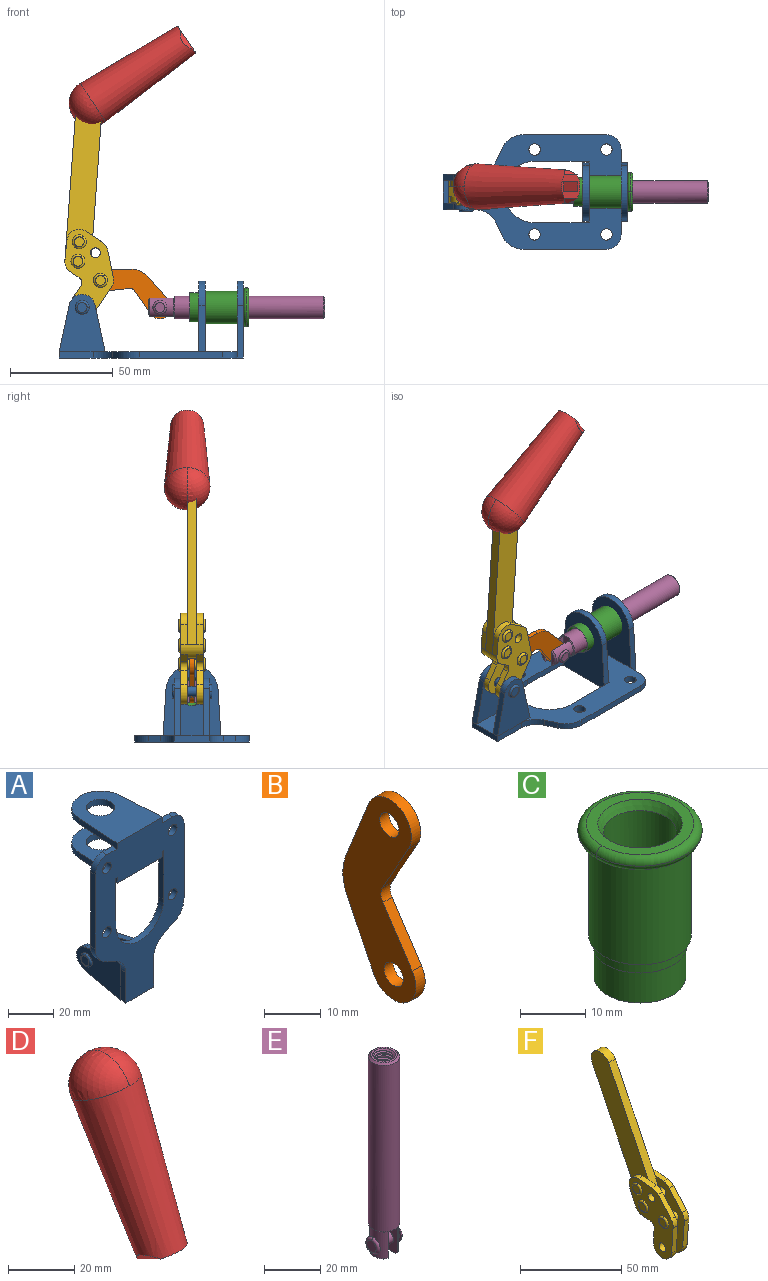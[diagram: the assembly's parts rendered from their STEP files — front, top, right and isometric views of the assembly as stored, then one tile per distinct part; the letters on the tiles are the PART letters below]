
ASSEMBLY  parts=6 mates=6
PART A: 55 faces, bbox 55.7x37.4x89.8 mm
  f0: torus R=2.41mm, axis (-1,0,0), area 15mm2, adj f11,f15,f25
  f1: torus R=2.41mm, axis (-1,0,0), area 15mm2, adj f10,f12,f22
  f2: cylinder r=2.78mm len=5.56mm, axis (0,-1,0), area 54.2mm2, adj f30,f54
  f3: cylinder r=14.99mm len=29.97mm, axis (0,-1,0), area 145.9mm2, adj f30,f49,f53,f54
  f4: cylinder r=2.78mm len=5.56mm, axis (0,-1,0), area 54.2mm2, adj f30,f54
  f5: cylinder r=2.78mm len=5.56mm, axis (0,-1,0), area 54.2mm2, adj f30,f54
  f6: cylinder r=2.78mm len=5.56mm, axis (0,-1,0), area 54.2mm2, adj f30,f54
  f7: cylinder r=6.35mm len=12.7mm, axis (0,0,1), area 123.6mm2, adj f27,f51
  f8: cylinder r=6.35mm len=12.7mm, axis (0,0,-1), area 124.7mm2, adj f21,f35
  f9: cylinder r=2.41mm len=11.18mm, axis (-1,0,0), area 169.4mm2, adj f16,f19
  f10: plane 4.83x4.83mm, normal (1,0,0), area 18.3mm2, adj f1,f12
  f11: plane 4.83x4.83mm, normal (-1,0,0), area 18.3mm2, adj f0,f15
  f12: torus R=2.41mm, axis (-1,0,0), area 15mm2, adj f1,f10,f22
  f13: cylinder r=6.35mm len=12.41mm, axis (1,0,0), area 53.4mm2, adj f18,f19,f22,f23
  f14: cylinder r=6.35mm len=12.41mm, axis (-1,0,0), area 53.4mm2, adj f16,f17,f24,f25
  f15: torus R=2.41mm, axis (-1,0,0), area 15mm2, adj f0,f11,f25
  f16: plane 27.86x22.35mm, normal (1,0,0), area 425.4mm2, adj f9,f14,f17,f24,f30
  f17: plane 22.86x4.97mm, normal (0,0.21,0.98), area 72.5mm2, adj f14,f16,f25,f30
  f18: plane 22.86x4.97mm, normal (0,0.21,0.98), area 72.5mm2, adj f13,f19,f22,f30
  f19: plane 27.86x22.35mm, normal (-1,0,0), area 425.4mm2, adj f9,f13,f18,f23,f30
  f20: cylinder r=12.7mm len=25.35mm, axis (0,0,-1), area 119.8mm2, adj f21,f34,f35,f36
  f21: plane 34.21x28.07mm, normal (0,0,-1), area 702.4mm2, adj f8,f20,f30,f34,f36
  f22: plane 27.96x22.45mm, normal (1,0,0), area 407.2mm2, adj f1,f12,f13,f18,f23,f30,f42,f43
  f23: plane 22.86x4.97mm, normal (0,0.21,-0.98), area 72.5mm2, adj f13,f19,f22,f44
  f24: plane 22.86x4.97mm, normal (0,0.21,-0.98), area 72.5mm2, adj f14,f16,f25,f44
  f25: plane 27.86x22.35mm, normal (-1,0,0), area 407.1mm2, adj f0,f14,f15,f17,f24,f30,f45,f46
  f26: plane 3.1x0.95mm, normal (0,0,-1), area 2.7mm2, adj f30,f49,f50,f54
  f27: plane 34.21x28.07mm, normal (0,0,1), area 702.4mm2, adj f7,f28,f30,f50,f52
  f28: cylinder r=12.7mm len=25.35mm, axis (0,0,1), area 118.8mm2, adj f27,f50,f51,f52
  f29: plane 3.1x0.95mm, normal (0,0,-1), area 2.7mm2, adj f30,f52,f53,f54
  f30: plane 86.54x55.63mm, normal (0,1,0), area 2362.9mm2, adj f2,f3,f4,f5,f6,f16,f17,f18
  f31: plane 40.56x3.1mm, normal (-1,0,0), area 125.7mm2, adj f30,f32,f48,f54
  f32: cylinder r=7.11mm len=7.11mm, axis (0,-1,0), area 34.6mm2, adj f30,f31,f33,f54
  f33: plane 6.67x3.1mm, normal (0,0,1), area 20.4mm2, adj f30,f32,f34,f54
  f34: plane 25.39x3.13mm, normal (-1,0.06,0), area 79.5mm2, adj f20,f21,f33,f35,f54
  f35: plane 37.31x28.45mm, normal (0,0,1), area 789.9mm2, adj f8,f20,f34,f36,f54
  f36: plane 25.39x3.13mm, normal (1,0.06,0), area 79.5mm2, adj f20,f21,f35,f37,f54
  f37: plane 6.67x3.1mm, normal (0,0,1), area 20.4mm2, adj f30,f36,f38,f54
  f38: cylinder r=7.11mm len=7.11mm, axis (0,-1,0), area 34.6mm2, adj f30,f37,f39,f54
  f39: plane 40.56x3.1mm, normal (1,0,0), area 125.7mm2, adj f30,f38,f40,f54
  f40: cylinder r=11.18mm len=10.16mm, axis (0,-1,0), area 39.5mm2, adj f30,f39,f41,f54
  f41: plane 6.09x3.1mm, normal (0.42,0,-0.91), area 20.8mm2, adj f30,f40,f42,f54
  f42: cylinder r=11.18mm len=9.41mm, axis (0,-1,0), area 37.2mm2, adj f22,f30,f41,f43,f54
  f43: plane 16.5x3.1mm, normal (1,0,0), area 51.1mm2, adj f22,f42,f44,f54
  f44: plane 17.37x3.1mm, normal (0,0,-1), area 53.8mm2, adj f23,f24,f30,f43,f45,f54
  f45: plane 16.5x3.1mm, normal (-1,0,0), area 51.1mm2, adj f25,f44,f46,f54
  f46: cylinder r=11.18mm len=9.41mm, axis (0,-1,0), area 37.2mm2, adj f25,f30,f45,f47,f54
  f47: plane 6.09x3.1mm, normal (-0.42,0,-0.91), area 20.8mm2, adj f30,f46,f48,f54
  f48: cylinder r=11.18mm len=10.16mm, axis (0,-1,0), area 39.5mm2, adj f30,f31,f47,f54
  f49: plane 26.54x3.1mm, normal (-1,0,0), area 82.3mm2, adj f3,f26,f30,f54
  f50: plane 25.39x3.1mm, normal (1,0.06,0), area 78.8mm2, adj f26,f27,f28,f51,f54
  f51: plane 37.31x28.45mm, normal (0,0,-1), area 789.9mm2, adj f7,f28,f50,f52,f54
  f52: plane 25.39x3.1mm, normal (-1,0.06,0), area 78.8mm2, adj f27,f28,f29,f51,f54
  f53: plane 26.54x3.1mm, normal (1,0,0), area 82.3mm2, adj f3,f29,f30,f54
  f54: plane 89.66x55.63mm, normal (0,-1,0), area 2678.5mm2, adj f2,f3,f4,f5,f6,f26,f29,f31
PART B: 12 faces, bbox 2.3x18.2x42.8 mm
  f0: cylinder r=2.4mm len=4.8mm, axis (1,0,0), area 34.9mm2, adj f4,f11
  f1: cylinder r=10.41mm len=8.47mm, axis (1,0,0), area 20.2mm2, adj f4,f9,f10,f11
  f2: cylinder r=3.05mm len=3.16mm, axis (1,0,0), area 7.7mm2, adj f4,f6,f7,f11
  f3: cylinder r=2.4mm len=4.8mm, axis (1,0,0), area 34.9mm2, adj f4,f11
  f4: plane 42.81x18.23mm, normal (-1,0,0), area 414.1mm2, adj f0,f1,f2,f3,f5,f6,f7,f8
  f5: cylinder r=5.54mm len=10.67mm, axis (1,0,0), area 41.8mm2, adj f4,f6,f10,f11
  f6: plane 11.66x6.53mm, normal (0,-0.87,-0.49), area 30.9mm2, adj f2,f4,f5,f11
  f7: plane 11.17x7.33mm, normal (0,-0.84,0.55), area 30.9mm2, adj f2,f4,f8,f11
  f8: cylinder r=5.54mm len=10.51mm, axis (1,0,0), area 41.8mm2, adj f4,f7,f9,f11
  f9: plane 13.67x6.67mm, normal (0,0.9,-0.44), area 35.1mm2, adj f1,f4,f8,f11
  f10: plane 14.1x5.7mm, normal (0,0.93,0.37), area 35.1mm2, adj f1,f4,f5,f11
  f11: plane 42.81x18.23mm, normal (1,0,0), area 414.1mm2, adj f0,f1,f2,f3,f5,f6,f7,f8
PART C: 15 faces, bbox 20.6x20.6x28.7 mm
  f0: torus R=8.26mm, axis (0,0,1), area 56.8mm2, adj f1,f10,f12
  f1: torus R=8.26mm, axis (0,0,1), area 56.8mm2, adj f0,f6,f13
  f2: cylinder r=5.59mm len=25.91mm, axis (0,0,1), area 909.6mm2, adj f3,f4
  f3: cone r=6.86mm half-angle=45deg, axis (0,0,-1), area 70.2mm2, adj f2,f14
  f4: cone r=6.47mm half-angle=30deg, axis (0,0,1), area 66.7mm2, adj f2,f13
  f5: cylinder r=7.04mm len=14.07mm, axis (0,0,1), area 252.6mm2, adj f11,f14
  f6: torus R=8.26mm, axis (0,0,1), area 56.8mm2, adj f1,f12,f13
  f7: cylinder r=7.16mm len=14.33mm, axis (0,0,1), area 91.5mm2, adj f9,f11
  f8: cylinder r=7.86mm len=18.42mm, axis (0,0,1), area 909.6mm2, adj f9,f10
  f9: plane 15.72x15.72mm, normal (0,0,-1), area 33mm2, adj f7,f8
  f10: plane 16.51x16.51mm, normal (0,0,-1), area 19.9mm2, adj f0,f8,f12
  f11: plane 14.33x14.33mm, normal (0,0,-1), area 5.7mm2, adj f5,f7
  f12: torus R=8.26mm, axis (0,0,1), area 56.8mm2, adj f0,f6,f10
  f13: plane 16.51x16.51mm, normal (0,0,1), area 82.7mm2, adj f1,f4,f6
  f14: plane 14.07x14.07mm, normal (0,0,-1), area 7.8mm2, adj f3,f5
PART D: 11 faces, bbox 22.3x42.6x64.5 mm
  f0: sphere r=11.13mm, area 411.4mm2, adj f1,f8
  f1: cone r=11.11mm half-angle=3.3deg, axis (0,0.44,0.9), area 3251.8mm2, adj f0,f7,f8,f9,f10
  f2: cylinder r=6.16mm len=11.7mm, axis (1,0,0), area 89.5mm2, adj f3,f4,f5,f6
  f3: plane 60.23x36.75mm, normal (-1,0,0), area 763.6mm2, adj f2,f4,f6,f10
  f4: plane 51.37x25.05mm, normal (0,0.9,-0.44), area 264.2mm2, adj f2,f3,f5,f10
  f5: plane 60.23x36.75mm, normal (1,0,0), area 763.6mm2, adj f2,f4,f6,f10
  f6: plane 51.37x25.05mm, normal (0,-0.9,0.44), area 264.2mm2, adj f2,f3,f5,f10
  f7: plane 9.95x5.95mm, normal (0.71,-0.31,-0.64), area 25.8mm2, adj f1,f10
  f8: sphere r=11.13mm, area 411.4mm2, adj f0,f1
  f9: plane 9.95x5.95mm, normal (-0.71,-0.31,-0.64), area 25.8mm2, adj f1,f10
  f10: plane 14.27x11.38mm, normal (0,-0.44,-0.9), area 106.7mm2, adj f1,f3,f4,f5,f6,f7,f9
PART E: 48 faces, bbox 12.6x11.1x86.1 mm
  f0: torus R=2.41mm, axis (-1,0,0), area 15mm2, adj f30,f32,f34
  f1: torus R=2.41mm, axis (-1,0,0), area 15mm2, adj f29,f31,f33
  f2: cylinder r=5.54mm len=72.39mm, axis (0,0,1), area 2518.5mm2, adj f3,f4,f42,f43
  f3: cone r=5.54mm half-angle=45deg, axis (0,0,1), area 7.6mm2, adj f2,f5,f41
  f4: cone r=5.54mm half-angle=45deg, axis (0,0,-1), area 34.9mm2, adj f2,f39
  f5: cylinder r=5.08mm len=11.48mm, axis (0,0,1), area 108.3mm2, adj f3,f7,f8,f41
  f6: cylinder r=2.41mm len=4.83mm, axis (-1,0,0), area 71.2mm2, adj f40,f41
  f7: cylinder r=2.41mm len=4.83mm, axis (-1,0,0), area 7.6mm2, adj f5,f34
  f8: cone r=5.08mm half-angle=45deg, axis (0,0,1), area 10.6mm2, adj f5,f37,f41
  f9: cone r=3.98mm half-angle=45deg, axis (0,0,1), area 17.6mm2, adj f27,f39,f45,f46,f47
  f10: cylinder r=2.41mm len=4.83mm, axis (-1,0,0), area 7.6mm2, adj f33,f38
  f11: cylinder r=3.2mm len=6.4mm, axis (0,0,1), area 78.4mm2, adj f12,f28,f44,f45,f47
  f12: cylinder r=3.2mm len=6.4mm, axis (0,0,1), area 10.5mm2, adj f11,f13,f45,f47
  f13: cylinder r=3.2mm len=6.4mm, axis (0,0,1), area 10.5mm2, adj f12,f14,f45,f47
  f14: cylinder r=3.2mm len=6.4mm, axis (0,0,1), area 10.5mm2, adj f13,f15,f45,f47
  f15: cylinder r=3.2mm len=6.4mm, axis (0,0,1), area 10.5mm2, adj f14,f16,f45,f47
  f16: cylinder r=3.2mm len=6.4mm, axis (0,0,1), area 10.5mm2, adj f15,f17,f45,f47
  f17: cylinder r=3.2mm len=6.4mm, axis (0,0,1), area 10.5mm2, adj f16,f18,f45,f47
  f18: cylinder r=3.2mm len=6.4mm, axis (0,0,1), area 10.5mm2, adj f17,f19,f45,f47
  f19: cylinder r=3.2mm len=6.4mm, axis (0,0,1), area 10.5mm2, adj f18,f20,f45,f47
  f20: cylinder r=3.2mm len=6.4mm, axis (0,0,1), area 10.5mm2, adj f19,f21,f45,f47
  f21: cylinder r=3.2mm len=6.4mm, axis (0,0,1), area 10.5mm2, adj f20,f22,f45,f47
  f22: cylinder r=3.2mm len=6.4mm, axis (0,0,1), area 10.5mm2, adj f21,f23,f45,f47
  f23: cylinder r=3.2mm len=6.4mm, axis (0,0,1), area 10.5mm2, adj f22,f24,f45,f47
  f24: cylinder r=3.2mm len=6.4mm, axis (0,0,1), area 10.5mm2, adj f23,f25,f45,f47
  f25: cylinder r=3.2mm len=6.4mm, axis (0,0,1), area 10.5mm2, adj f24,f26,f45,f47
  f26: cylinder r=3.2mm len=6.4mm, axis (0,0,1), area 10.5mm2, adj f25,f27,f45,f47
  f27: cylinder r=3.2mm len=6.4mm, axis (0,0,1), area 7.4mm2, adj f9,f26,f45,f47
  f28: cone r=3.2mm half-angle=60deg, axis (0,0,1), area 37.2mm2, adj f11
  f29: plane 4.83x4.83mm, normal (-1,0,0), area 18.3mm2, adj f1,f31
  f30: plane 4.83x4.83mm, normal (1,0,0), area 18.3mm2, adj f0,f32
  f31: torus R=2.41mm, axis (-1,0,0), area 15mm2, adj f1,f29,f33
  f32: torus R=2.41mm, axis (-1,0,0), area 15mm2, adj f0,f30,f34
  f33: plane 6.83x6.83mm, normal (1,0,0), area 18.3mm2, adj f1,f10,f31
  f34: plane 6.83x6.83mm, normal (-1,0,0), area 18.3mm2, adj f0,f7,f32
  f35: cone r=5.08mm half-angle=45deg, axis (0,0,1), area 10.6mm2, adj f36,f38,f40
  f36: plane 7.25x1.97mm, normal (0,0,-1), area 10mm2, adj f35,f40
  f37: plane 7.25x1.97mm, normal (0,0,-1), area 10mm2, adj f8,f41
  f38: cylinder r=5.08mm len=11.48mm, axis (0,0,1), area 108.3mm2, adj f10,f35,f40,f42
  f39: plane 9.55x9.55mm, normal (0,0,1), area 22mm2, adj f4,f9
  f40: plane 12.76x10.09mm, normal (1,0,0), area 95.7mm2, adj f6,f35,f36,f38,f42,f43
  f41: plane 12.76x10.09mm, normal (-1,0,0), area 95.7mm2, adj f3,f5,f6,f8,f37,f43
  f42: cone r=5.54mm half-angle=45deg, axis (0,0,1), area 7.6mm2, adj f2,f38,f40
  f43: plane 11.07x4.7mm, normal (0,0,-1), area 50.4mm2, adj f2,f40,f41
  f44: plane 0.89x0.62mm, normal (-1,0,0), area 0.3mm2, adj f11,f45,f46,f47
  f45: bspline ~24.8x7.63mm, area 266.6mm2, adj f9,f11,f12,f13,f14,f15,f16,f17
  f46: bspline ~24.87x7.63mm, area 73.6mm2, adj f9,f44,f45,f47
  f47: bspline ~24.98x7.63mm, area 272.5mm2, adj f9,f11,f12,f13,f14,f15,f16,f17
PART F: 59 faces, bbox 12.9x60.2x99.6 mm
  f0: torus R=2.39mm, axis (-1,0,0), area 14.9mm2, adj f20,f43,f51
  f1: torus R=2.39mm, axis (-1,0,0), area 14.9mm2, adj f19,f42,f51
  f2: torus R=2.39mm, axis (-1,0,0), area 14.9mm2, adj f18,f35,f51
  f3: torus R=2.39mm, axis (-1,0,0), area 14.9mm2, adj f14,f17,f23
  f4: torus R=2.39mm, axis (-1,0,0), area 14.9mm2, adj f13,f16,f23
  f5: torus R=2.39mm, axis (-1,0,0), area 14.9mm2, adj f12,f15,f23
  f6: cylinder r=2.39mm len=4.78mm, axis (1,0,0), area 46.5mm2, adj f48,f50,f51
  f7: cylinder r=2.39mm len=4.78mm, axis (1,0,0), area 46.5mm2, adj f50,f51
  f8: cylinder r=6.35mm len=12.68mm, axis (1,0,0), area 61.8mm2, adj f38,f39,f50,f51
  f9: cylinder r=2.39mm len=4.78mm, axis (-1,0,0), area 70.5mm2, adj f46,f50
  f10: cylinder r=2.39mm len=4.78mm, axis (-1,0,0), area 46.5mm2, adj f23,f45,f46
  f11: cylinder r=2.39mm len=4.78mm, axis (-1,0,0), area 46.5mm2, adj f23,f46
  f12: plane 4.78x4.78mm, normal (1,0,0), area 17.9mm2, adj f5,f15
  f13: plane 4.78x4.78mm, normal (1,0,0), area 17.9mm2, adj f4,f16
  f14: plane 4.78x4.78mm, normal (1,0,0), area 17.9mm2, adj f3,f17
  f15: torus R=2.39mm, axis (-1,0,0), area 14.9mm2, adj f5,f12,f23
  f16: torus R=2.39mm, axis (-1,0,0), area 14.9mm2, adj f4,f13,f23
  f17: torus R=2.39mm, axis (-1,0,0), area 14.9mm2, adj f3,f14,f23
  f18: plane 4.78x4.78mm, normal (-1,0,0), area 17.9mm2, adj f2,f35
  f19: plane 4.78x4.78mm, normal (-1,0,0), area 17.9mm2, adj f1,f42
  f20: plane 4.78x4.78mm, normal (-1,0,0), area 17.9mm2, adj f0,f43
  f21: plane 2.26x0.2mm, normal (1,0,0), area 0.2mm2, adj f31,f44
  f22: plane 2.26x0.2mm, normal (-1,0,0), area 0.2mm2, adj f41,f44
  f23: plane 39.37x30.77mm, normal (1,0,0), area 565.5mm2, adj f3,f4,f5,f10,f11,f15,f16,f17
  f24: cylinder r=6.1mm len=4.15mm, axis (-1,0,0), area 14.7mm2, adj f23,f25,f32,f46
  f25: plane 10.25x9.01mm, normal (0,-0.75,0.66), area 42.3mm2, adj f23,f24,f26,f46
  f26: cylinder r=6.35mm len=4.64mm, axis (-1,0,0), area 15.6mm2, adj f23,f25,f27,f46
  f27: plane 15.84x3.1mm, normal (0,-1,-0.07), area 49.2mm2, adj f23,f26,f28,f46
  f28: cylinder r=6.35mm len=12.68mm, axis (-1,0,0), area 61.8mm2, adj f23,f27,f29,f46
  f29: plane 8.11x3.1mm, normal (0,1,0.07), area 25.2mm2, adj f23,f28,f30,f46
  f30: cylinder r=3.05mm len=3.25mm, axis (-1,0,0), area 14.8mm2, adj f23,f29,f31,f46
  f31: plane 5.99x3.1mm, normal (0,0.07,-1), area 18.6mm2, adj f21,f23,f30,f44,f46
  f32: plane 9.5x3.1mm, normal (0,-0.07,1), area 29.5mm2, adj f23,f24,f33,f46,f47
  f33: cylinder r=6.1mm len=8.63mm, axis (-1,0,0), area 39.1mm2, adj f23,f32,f34,f47
  f34: plane 8.65x3.96mm, normal (0,0.91,-0.42), area 29.5mm2, adj f23,f33,f44,f47
  f35: torus R=2.39mm, axis (-1,0,0), area 14.9mm2, adj f2,f18,f51
  f36: plane 10.25x9.01mm, normal (0,-0.75,0.66), area 42.3mm2, adj f37,f49,f50,f51
  f37: cylinder r=6.35mm len=4.64mm, axis (1,0,0), area 15.6mm2, adj f36,f38,f50,f51
  f38: plane 15.84x3.1mm, normal (0,-1,-0.07), area 49.2mm2, adj f8,f37,f50,f51
  f39: plane 8.11x3.1mm, normal (0,1,0.07), area 25.2mm2, adj f8,f40,f50,f51
  f40: cylinder r=3.05mm len=3.25mm, axis (1,0,0), area 14.8mm2, adj f39,f41,f50,f51
  f41: plane 5.99x3.1mm, normal (0,0.07,-1), area 18.6mm2, adj f22,f40,f44,f50,f51
  f42: torus R=2.39mm, axis (-1,0,0), area 14.9mm2, adj f1,f19,f51
  f43: torus R=2.39mm, axis (-1,0,0), area 14.9mm2, adj f0,f20,f51
  f44: cylinder r=6.35mm len=12.12mm, axis (-1,0,0), area 128.9mm2, adj f21,f22,f23,f31,f34,f41,f46,f47
  f45: plane 2.65x1.35mm, normal (1,0,0), area 1mm2, adj f10,f55
  f46: plane 39.08x20.42mm, normal (-1,0,0), area 412.5mm2, adj f9,f10,f11,f24,f25,f26,f27,f28
  f47: plane 77.62x39.82mm, normal (1,0,0), area 850mm2, adj f32,f33,f34,f44,f53,f54,f55
  f48: plane 2.65x1.35mm, normal (-1,0,0), area 1mm2, adj f6,f55
  f49: cylinder r=6.1mm len=4.15mm, axis (1,0,0), area 14.7mm2, adj f36,f50,f51,f56
  f50: plane 39.08x20.42mm, normal (1,0,0), area 412.5mm2, adj f6,f7,f8,f9,f36,f37,f38,f39
  f51: plane 39.37x30.77mm, normal (-1,0,0), area 565.5mm2, adj f0,f1,f2,f6,f7,f8,f35,f36
  f52: plane 8.65x3.96mm, normal (0,0.91,-0.42), area 29.5mm2, adj f44,f51,f57,f58
  f53: plane 68.49x33.4mm, normal (0,0.9,-0.44), area 358.1mm2, adj f44,f47,f54,f58
  f54: cylinder r=6.35mm len=12.06mm, axis (1,0,0), area 93.7mm2, adj f47,f53,f55,f58
  f55: plane 68.49x33.4mm, normal (0,-0.9,0.44), area 358.1mm2, adj f44,f45,f46,f47,f48,f50,f54,f58
  f56: plane 9.5x3.1mm, normal (0,-0.07,1), area 29.5mm2, adj f49,f50,f51,f57,f58
  f57: cylinder r=6.1mm len=8.63mm, axis (1,0,0), area 39.1mm2, adj f51,f52,f56,f58
  f58: plane 77.62x39.82mm, normal (-1,0,0), area 850mm2, adj f44,f52,f53,f54,f55,f56,f57
PLACE A rot(axis=(0.58,0.58,0.58),120deg) t=(-37.27,1.74,0.1)mm fixed
PLACE B rot(axis=(0.49,-0.49,-0.73),108deg) t=(-55.56,1.74,9.19)mm
PLACE C rot(axis=(0,1,0),90deg) t=(-37.27,-22.87,24.71)mm
PLACE D rot(axis=(0.69,-0.69,-0.19),158.8deg) t=(23.01,4.09,134.86)mm
PLACE E rot(axis=(0.58,0.58,0.58),120deg) t=(-47.03,1.74,0.1)mm
PLACE F rot(axis=(0.25,0.25,0.93),93.9deg) t=(-31.97,1.74,40.11)mm
MATE revolute B.f5 <-> F.f4  axis (0,-1,0) through (-60.46,1.74,37.85)mm
MATE revolute A.f0 <-> F.f7  axis (0,-1,0) through (-69.37,1.74,24.71)mm
MATE fastened C.f0 <-> A.f7  axis (-1,0,0) through (9.12,1.74,24.71)mm
MATE fastened F.f54 <-> D.f2  axis (0,1,0) through (-65.92,4.09,123.14)mm
MATE slider E.f2 <-> C.f2  axis (1,0,0) through (11.75,1.74,24.71)mm
MATE revolute B.f3 <-> E.f6  axis (0,-1,0) through (-31.56,1.74,24.71)mm
